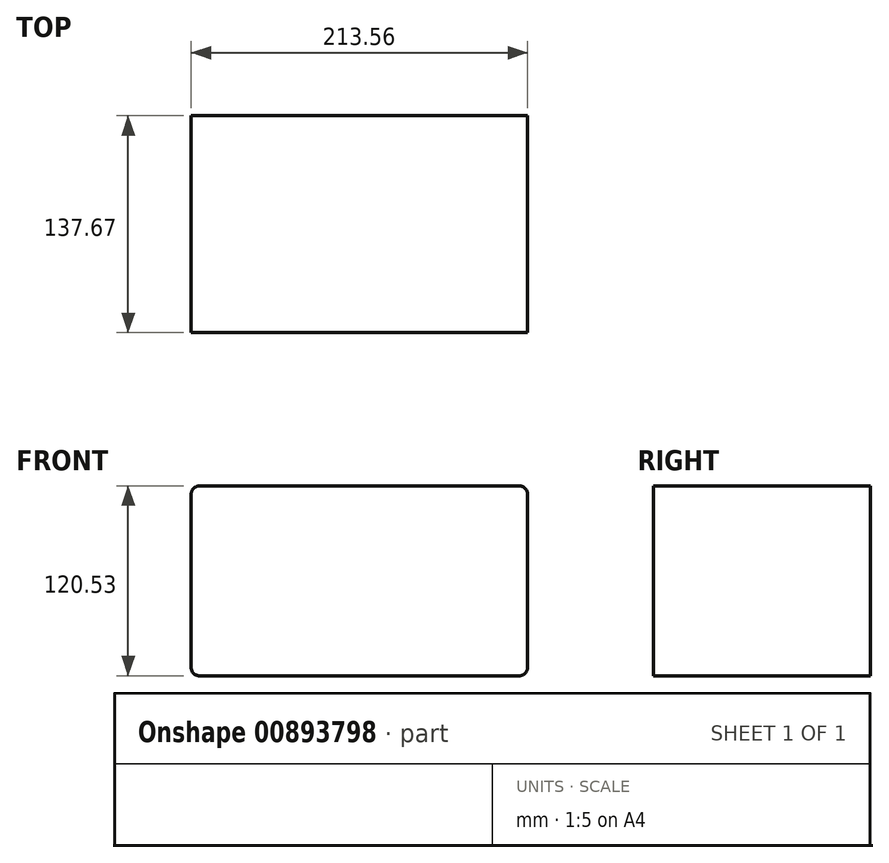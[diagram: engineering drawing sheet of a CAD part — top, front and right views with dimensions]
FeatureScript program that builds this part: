
annotation { "Feature Type Name" : "Feature", "Feature Type Description" : "" }
export const myFeature = defineFeature(function(context is Context, id is Id, definition is map)
    precondition{}
    {
        {
            var Q0;
            Q0=qCreatedBy(makeId("Front.planeOp"),FACE);
            var sketch = newSketch(context, id + "F0", { "sketchPlane" : qUnion([Q0])});
            skLineSegment(sketch, "E0.bottom", {"start": v(-112.4, 49.43) * mm, "end": v(101.15, 49.43) * mm});
            skLineSegment(sketch, "E0.top", {"start": v(-112.4, -71.1) * mm, "end": v(101.15, -71.1) * mm});
            skLineSegment(sketch, "E0.left", {"start": v(-112.4, 49.43) * mm, "end": v(-112.4, -71.1) * mm});
            skLineSegment(sketch, "E0.right", {"start": v(101.15, 49.43) * mm, "end": v(101.15, -71.1) * mm});
            skSolve(sketch);
        }
        {
            var Q0;
            Q0=makeQuery(id+"F0.imprint","IMPRINT",FACE,{"disambiguationData":[TD([[makeQuery(id+"F0.imprint","IMPRINT",EDGE,{"derivedFrom":sQuery(id+"F0.wireOp",EDGE,"E0.bottom")}),-1.0]])]});
            extrude(context, id + "F1", {"entities" : qUnion([Q0]), "oppositeDirection" : true, "depth" : 137.67 * mm, "offsetDistance" : 25.4 * mm});
        }
        {
            var Q0;
            Q0=makeQuery(id+"F1.opExtrude","SWEPT_EDGE",EDGE,{"disambiguationData":[OSD([sQuery(id+"F0.wireOp",EDGE,"E0.bottom"),sQuery(id+"F0.wireOp",EDGE,"E0.right")])]});
            var Q1;
            Q1=makeQuery(id+"F1.opExtrude","SWEPT_EDGE",EDGE,{"disambiguationData":[OSD([sQuery(id+"F0.wireOp",EDGE,"E0.top"),sQuery(id+"F0.wireOp",EDGE,"E0.right")])]});
            var Q2;
            Q2=makeQuery(id+"F1.opExtrude","SWEPT_EDGE",EDGE,{"disambiguationData":[OSD([sQuery(id+"F0.wireOp",EDGE,"E0.bottom"),sQuery(id+"F0.wireOp",EDGE,"E0.left")])]});
            var Q3;
            Q3=makeQuery(id+"F1.opExtrude","SWEPT_EDGE",EDGE,{"disambiguationData":[OSD([sQuery(id+"F0.wireOp",EDGE,"E0.top"),sQuery(id+"F0.wireOp",EDGE,"E0.left")])]});
            fillet(context, id + "F2", {"entities" : qUnion([Q0, Q1, Q2, Q3]), "radius" : 5.08 * mm, "tangentPropagation" : true, "allowEdgeOverflow" : false});
        }
    });
